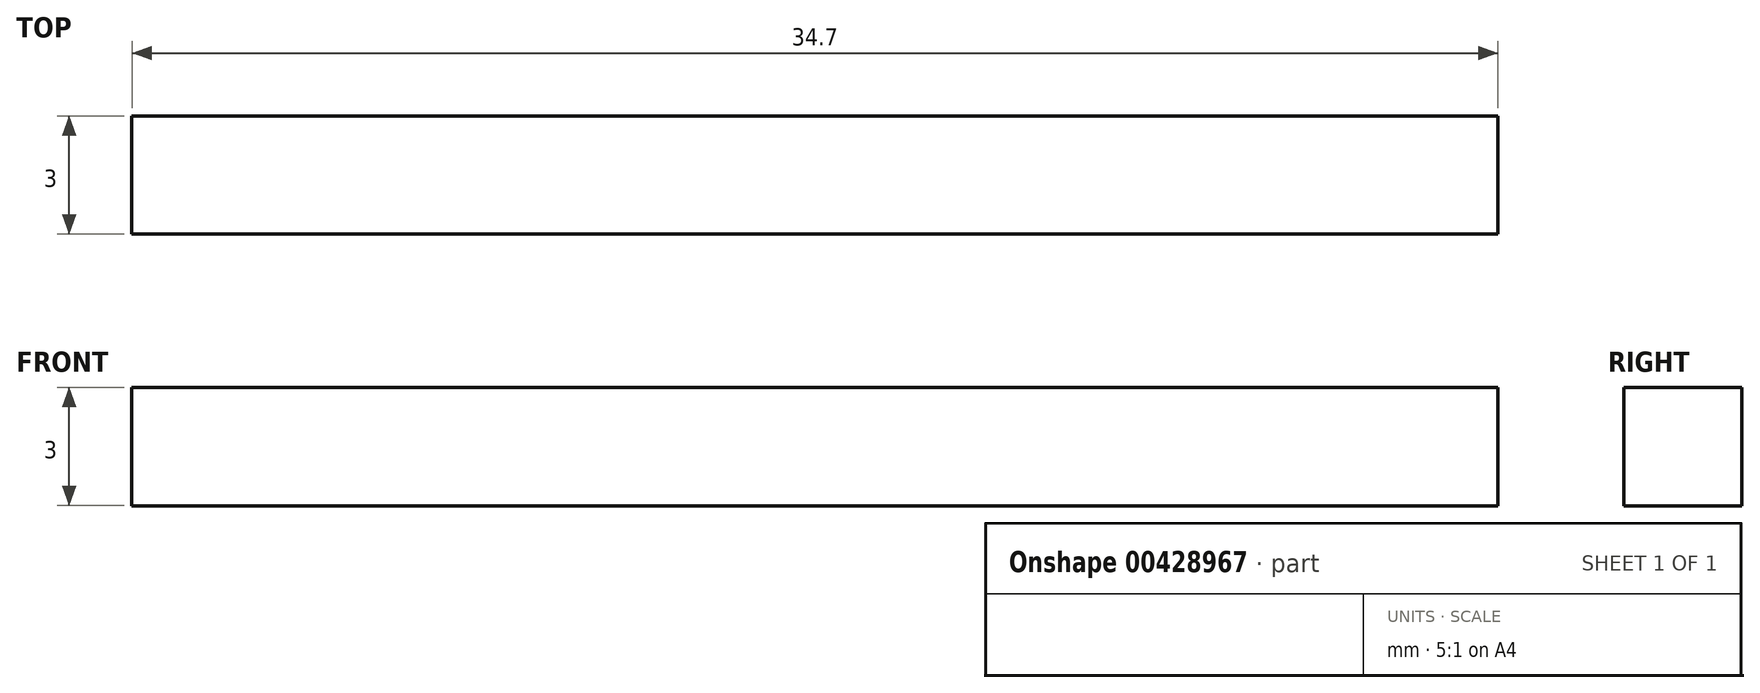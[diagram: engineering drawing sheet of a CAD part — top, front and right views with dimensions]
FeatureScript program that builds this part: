
annotation { "Feature Type Name" : "Feature", "Feature Type Description" : "" }
export const myFeature = defineFeature(function(context is Context, id is Id, definition is map)
    precondition{}
    {
        {
            var Q0;
            Q0=qCreatedBy(makeId("Front.planeOp"),FACE);
            var sketch = newSketch(context, id + "F0", { "sketchPlane" : qUnion([Q0])});
            skLineSegment(sketch, "E0", {"start": v(-16.91, 0.93) * mm, "end": v(17.79, 0.93) * mm});
            skLineSegment(sketch, "E1", {"start": v(17.79, 0.93) * mm, "end": v(17.79, -2.07) * mm});
            skLineSegment(sketch, "E2", {"start": v(17.79, -2.07) * mm, "end": v(-16.91, -2.07) * mm});
            skLineSegment(sketch, "E3", {"start": v(-16.91, -2.07) * mm, "end": v(-16.91, 0.93) * mm});
            skSolve(sketch);
        }
        {
            var Q0;
            Q0 = qSketchRegion(id + "F0", true);
            extrude(context, id + "F1", {"entities" : qUnion([Q0]), "depth" : 3 * mm});
        }
    });
